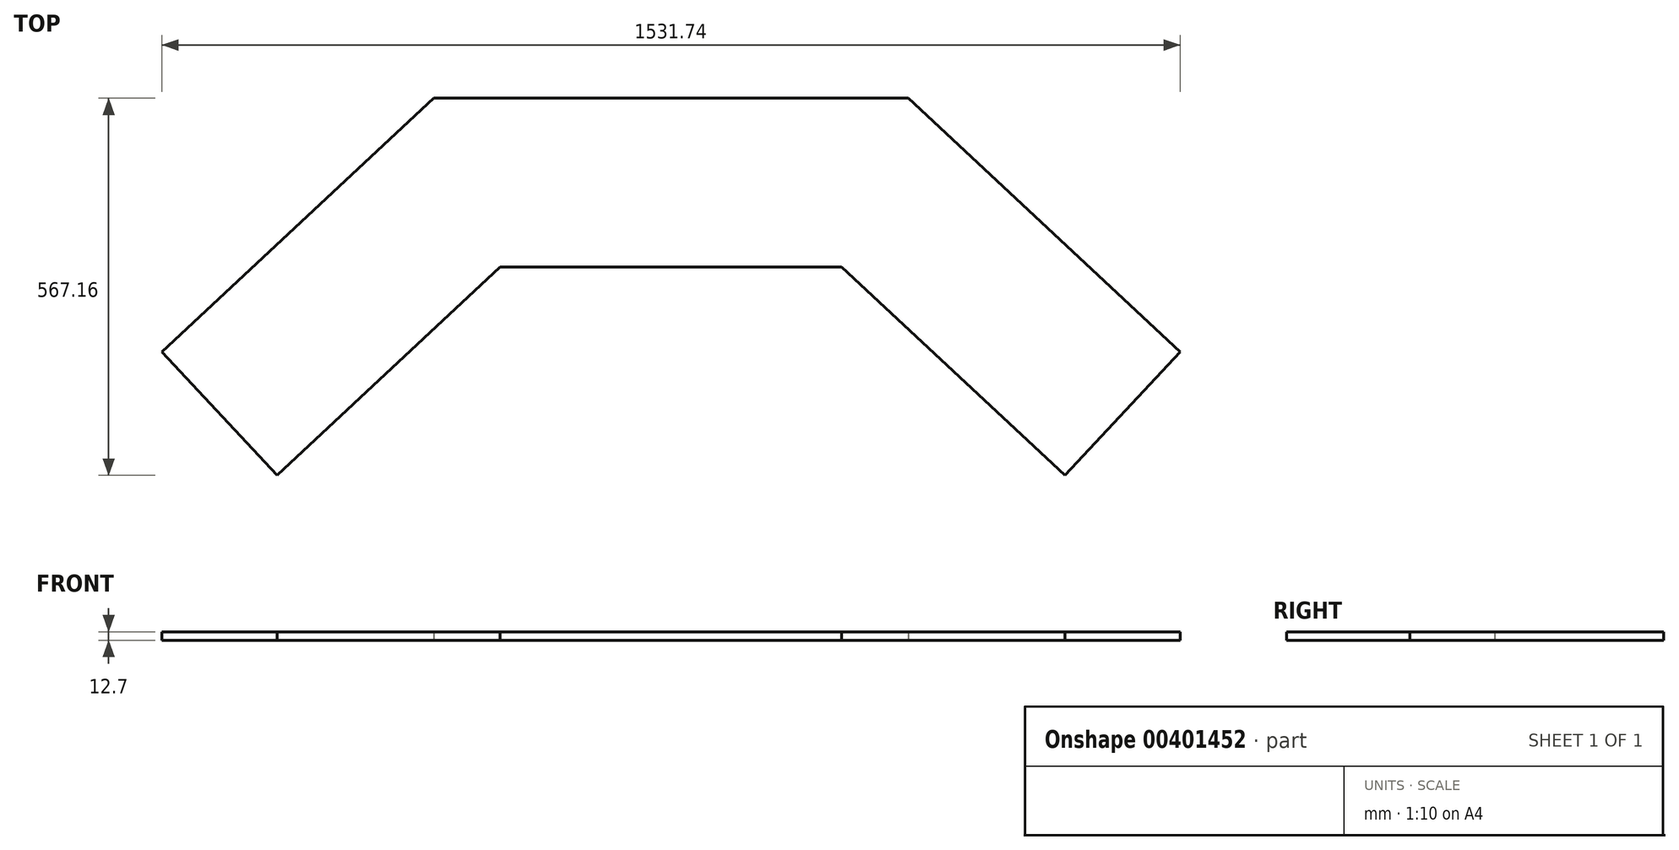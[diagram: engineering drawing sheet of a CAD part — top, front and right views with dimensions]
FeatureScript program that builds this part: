
annotation { "Feature Type Name" : "Feature", "Feature Type Description" : "" }
export const myFeature = defineFeature(function(context is Context, id is Id, definition is map)
    precondition{}
    {
        {
            var Q0;
            Q0=qCreatedBy(makeId("Top.planeOp"),FACE);
            var sketch = newSketch(context, id + "F0", { "sketchPlane" : qUnion([Q0])});
            skLineSegment(sketch, "E0", {"start": v(-356.87, 0) * mm, "end": v(356.87, 0) * mm});
            skLineSegment(sketch, "E1", {"start": v(356.87, 0) * mm, "end": v(765.87, -381.4) * mm});
            skLineSegment(sketch, "E2", {"start": v(765.87, -381.4) * mm, "end": v(592.65, -567.16) * mm});
            skLineSegment(sketch, "E3", {"start": v(-356.87, 0) * mm, "end": v(-765.87, -381.4) * mm});
            skLineSegment(sketch, "E4", {"start": v(-765.87, -381.4) * mm, "end": v(-592.64, -567.16) * mm});
            skLineSegment(sketch, "E5", {"start": v(0, 0) * mm, "end": v(0, -254) * mm});
            skLineSegment(sketch, "E6", {"start": v(0, -254) * mm, "end": v(-256.82, -254) * mm});
            skLineSegment(sketch, "E7", {"start": v(0, -254) * mm, "end": v(256.82, -254) * mm});
            skLineSegment(sketch, "E8", {"start": v(-592.64, -567.16) * mm, "end": v(-256.82, -254) * mm});
            skLineSegment(sketch, "E9", {"start": v(592.65, -567.16) * mm, "end": v(256.82, -254) * mm});
            skSolve(sketch);
        }
        {
            var Q0;
            {var subQ1=sQuery(id+"F0.wireOp",EDGE,"E3");Q0=makeQuery(id+"F0.imprint","IMPRINT",FACE,{"disambiguationData":[TD([[makeQuery(id+"F0.imprint","IMPRINT",EDGE,{"derivedFrom":subQ1}),1.0]])]});}
            var Q1;
            {var subQ0=sQuery(id+"F0.wireOp",EDGE,"E1");Q1=makeQuery(id+"F0.imprint","IMPRINT",FACE,{"disambiguationData":[TD([[makeQuery(id+"F0.imprint","IMPRINT",EDGE,{"derivedFrom":subQ0}),-1.0]])]});}
            extrude(context, id + "F1", {"entities" : qUnion([Q0, Q1]), "depth" : 12.7 * mm});
        }
    });
